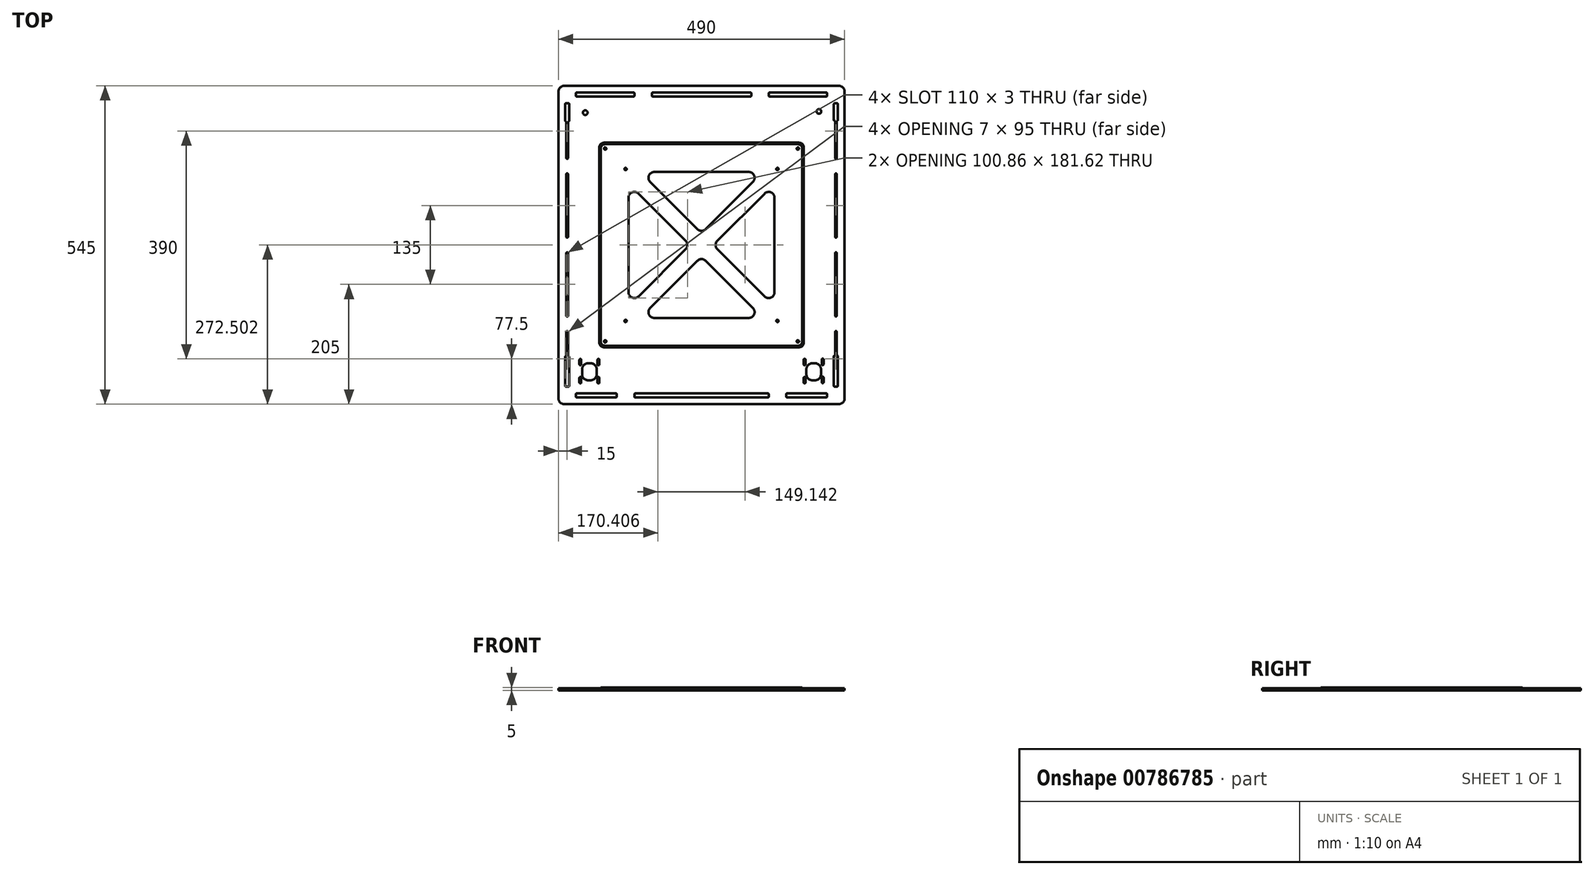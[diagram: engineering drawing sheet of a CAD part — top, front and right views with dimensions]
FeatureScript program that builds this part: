
annotation { "Feature Type Name" : "Feature", "Feature Type Description" : "" }
export const myFeature = defineFeature(function(context is Context, id is Id, definition is map)
    precondition{}
    {
        {
            var Q0;
            Q0=qCreatedBy(makeId("Top.planeOp"),FACE);
            var sketch = newSketch(context, id + "F0", { "sketchPlane" : qUnion([Q0])});
            skLineSegment(sketch, "E0", {"start": v(-83.5, 261) * mm, "end": v(83.54, 261) * mm});
            skLineSegment(sketch, "E1", {"start": v(116.54, 254) * mm, "end": v(213.54, 254) * mm});
            skLineSegment(sketch, "E2", {"start": v(115.04, 259.5) * mm, "end": v(115.04, 255.5) * mm});
            skLineSegment(sketch, "E3", {"start": v(-115, 259.5) * mm, "end": v(-115, 255.5) * mm});
            skArc(sketch, "E4", {"start": v(-226.5, 241) * mm, "mid": v(-226.94, 242.06) * mm, "end": v(-228, 242.5) * mm});
            skLineSegment(sketch, "E5", {"start": v(115, -255.5) * mm, "end": v(115, -259.5) * mm});
            skLineSegment(sketch, "E6", {"start": v(-115, -255.5) * mm, "end": v(-115, -259.5) * mm});
            skLineSegment(sketch, "E7", {"start": v(-179.5, -212.5) * mm, "end": v(-179.5, -221.5) * mm});
            skLineSegment(sketch, "E8", {"start": v(-204.5, -212.5) * mm, "end": v(-204.5, -221.5) * mm});
            skLineSegment(sketch, "E9", {"start": v(-209, -227.5) * mm, "end": v(-209, -235.5) * mm});
            skLineSegment(sketch, "E10", {"start": v(-207.5, -226) * mm, "end": v(-207.4, -226) * mm});
            skArc(sketch, "E11", {"start": v(230, 147.5) * mm, "mid": v(231.06, 147.94) * mm, "end": v(231.5, 149) * mm});
            skLineSegment(sketch, "E12", {"start": v(-205.9, -196.5) * mm, "end": v(-205.9, -204.5) * mm});
            skArc(sketch, "E13", {"start": v(-230, 122.5) * mm, "mid": v(-231.06, 122.06) * mm, "end": v(-231.5, 121) * mm});
            skLineSegment(sketch, "E14", {"start": v(-174.9, -196.5) * mm, "end": v(-174.9, -204.5) * mm});
            skLineSegment(sketch, "E15", {"start": v(-176.5, -206) * mm, "end": v(-176.4, -206) * mm});
            skLineSegment(sketch, "E16", {"start": v(204.5, -212.5) * mm, "end": v(204.5, -221.5) * mm});
            skLineSegment(sketch, "E17", {"start": v(179.5, -212.5) * mm, "end": v(179.5, -221.5) * mm});
            skLineSegment(sketch, "E18", {"start": v(209, -196.07) * mm, "end": v(209, -204.07) * mm});
            skLineSegment(sketch, "E19", {"start": v(207.4, -194.57) * mm, "end": v(207.5, -194.57) * mm});
            skLineSegment(sketch, "E20", {"start": v(178, -227.5) * mm, "end": v(178, -235.5) * mm});
            skLineSegment(sketch, "E21", {"start": v(176.4, -206) * mm, "end": v(176.5, -206) * mm});
            skLineSegment(sketch, "E22", {"start": v(228.5, -189.15) * mm, "end": v(228, -189.15) * mm});
            skLineSegment(sketch, "E23", {"start": v(-233.5, -191.65) * mm, "end": v(-233.5, -241) * mm});
            skLineSegment(sketch, "E24", {"start": v(-226.5, -191.65) * mm, "end": v(-226.5, -241) * mm});
            skLineSegment(sketch, "E25", {"start": v(-228.5, 211.47) * mm, "end": v(-228, 211.47) * mm});
            skLineSegment(sketch, "E26", {"start": v(-228.5, -190.15) * mm, "end": v(-228, -190.15) * mm});
            skLineSegment(sketch, "E27", {"start": v(228, 242.5) * mm, "end": v(232, 242.5) * mm});
            skLineSegment(sketch, "E28", {"start": v(228.5, -189.15) * mm, "end": v(228.5, -149) * mm});
            skLineSegment(sketch, "E29", {"start": v(146.5, -254) * mm, "end": v(213.5, -254) * mm});
            skLineSegment(sketch, "E30", {"start": v(231.5, -189.15) * mm, "end": v(231.5, -149) * mm});
            skLineSegment(sketch, "E31", {"start": v(-228.5, 211.47) * mm, "end": v(-228.5, 149) * mm});
            skLineSegment(sketch, "E32", {"start": v(-245, 262.5) * mm, "end": v(-245, -262.5) * mm});
            skLineSegment(sketch, "E33", {"start": v(245, 262.5) * mm, "end": v(245, -262.5) * mm});
            skLineSegment(sketch, "E34", {"start": v(-235, 272.5) * mm, "end": v(235, 272.5) * mm});
            skLineSegment(sketch, "E35", {"start": v(-213.5, -261) * mm, "end": v(-146.5, -261) * mm});
            skLineSegment(sketch, "E36", {"start": v(232, -242.5) * mm, "end": v(228, -242.5) * mm});
            skLineSegment(sketch, "E37", {"start": v(233.5, -241) * mm, "end": v(233.5, -190.65) * mm});
            skLineSegment(sketch, "E38", {"start": v(215, -255.5) * mm, "end": v(215, -259.5) * mm});
            skLineSegment(sketch, "E39", {"start": v(-226.5, 241) * mm, "end": v(-226.5, 212.97) * mm});
            skLineSegment(sketch, "E40", {"start": v(-172, -241) * mm, "end": v(-172, -194) * mm});
            skLineSegment(sketch, "E41", {"start": v(185, 242.5) * mm, "end": v(185, 222.5) * mm});
            skCircle(sketch, "E42", {"center": v(201, 228.5) * mm, "radius": 4 * mm});
            skLineSegment(sketch, "E43", {"start": v(-215, 205.9) * mm, "end": v(-215, 7.45) * mm});
            skArc(sketch, "E44", {"start": v(-209, -235.5) * mm, "mid": v(-208.56, -236.56) * mm, "end": v(-207.5, -237) * mm});
            skArc(sketch, "E45", {"start": v(-228.5, -14) * mm, "mid": v(-228.94, -12.94) * mm, "end": v(-230, -12.5) * mm});
            skLineSegment(sketch, "E46", {"start": v(-178, -227.5) * mm, "end": v(-178, -235.5) * mm});
            skLineSegment(sketch, "E47", {"start": v(-113.5, -254) * mm, "end": v(113.5, -254) * mm});
            skArc(sketch, "E48", {"start": v(-230, 12.5) * mm, "mid": v(-228.94, 12.94) * mm, "end": v(-228.5, 14) * mm});
            skLineSegment(sketch, "E49", {"start": v(-207.5, -195) * mm, "end": v(-207.4, -195) * mm});
            skArc(sketch, "E50", {"start": v(-228.5, 121) * mm, "mid": v(-228.94, 122.06) * mm, "end": v(-230, 122.5) * mm});
            skArc(sketch, "E51", {"start": v(-83.5, 261) * mm, "mid": v(-84.56, 260.56) * mm, "end": v(-85, 259.5) * mm});
            skArc(sketch, "E52", {"start": v(116.54, 261) * mm, "mid": v(115.48, 260.56) * mm, "end": v(115.04, 259.5) * mm});
            skLineSegment(sketch, "E53", {"start": v(174.9, -227.5) * mm, "end": v(174.9, -235.5) * mm});
            skArc(sketch, "E54", {"start": v(231.5, 121) * mm, "mid": v(231.06, 122.06) * mm, "end": v(230, 122.5) * mm});
            skArc(sketch, "E55", {"start": v(230, 12.5) * mm, "mid": v(231.06, 12.94) * mm, "end": v(231.5, 14) * mm});
            skLineSegment(sketch, "E56", {"start": v(226.5, 214.02) * mm, "end": v(226.5, 241) * mm});
            skLineSegment(sketch, "E57", {"start": v(207.4, -236.57) * mm, "end": v(207.5, -236.57) * mm});
            skArc(sketch, "E58", {"start": v(230, -122.5) * mm, "mid": v(231.06, -122.06) * mm, "end": v(231.5, -121) * mm});
            skArc(sketch, "E59", {"start": v(230, -147.5) * mm, "mid": v(228.94, -147.94) * mm, "end": v(228.5, -149) * mm});
            skArc(sketch, "E60", {"start": v(233.5, -190.65) * mm, "mid": v(233.06, -189.59) * mm, "end": v(232, -189.15) * mm});
            skLineSegment(sketch, "E61", {"start": v(189.5, -202.5) * mm, "end": v(194.5, -202.5) * mm});
            skArc(sketch, "E62", {"start": v(213.5, -261) * mm, "mid": v(214.56, -260.56) * mm, "end": v(215, -259.5) * mm});
            skArc(sketch, "E63", {"start": v(146.5, -254) * mm, "mid": v(145.44, -254.44) * mm, "end": v(145, -255.5) * mm});
            skArc(sketch, "E64", {"start": v(213.5, -192.5) * mm, "mid": v(214.56, -192.06) * mm, "end": v(215, -191) * mm});
            skArc(sketch, "E65", {"start": v(207.4, -225.57) * mm, "mid": v(206.34, -226) * mm, "end": v(205.9, -227.07) * mm});
            skArc(sketch, "E66", {"start": v(-228, 211.47) * mm, "mid": v(-226.94, 211.91) * mm, "end": v(-226.5, 212.97) * mm});
            skArc(sketch, "E67", {"start": v(174.9, -204.5) * mm, "mid": v(175.34, -205.56) * mm, "end": v(176.4, -206) * mm});
            skArc(sketch, "E68", {"start": v(178, -196.5) * mm, "mid": v(177.56, -195.44) * mm, "end": v(176.5, -195) * mm});
            skArc(sketch, "E69", {"start": v(207.5, -205.57) * mm, "mid": v(208.56, -205.13) * mm, "end": v(209, -204.07) * mm});
            skArc(sketch, "E70", {"start": v(-245, -262.5) * mm, "mid": v(-242.07, -269.57) * mm, "end": v(-235, -272.5) * mm});
            skArc(sketch, "E71", {"start": v(-194.5, -202.5) * mm, "mid": v(-201.57, -205.43) * mm, "end": v(-204.5, -212.5) * mm});
            skArc(sketch, "E72", {"start": v(204.5, -212.5) * mm, "mid": v(201.57, -205.43) * mm, "end": v(194.5, -202.5) * mm});
            skArc(sketch, "E73", {"start": v(-195, 212.5) * mm, "mid": v(-187.93, 215.43) * mm, "end": v(-185, 222.5) * mm});
            skArc(sketch, "E74", {"start": v(185, 222.5) * mm, "mid": v(187.93, 215.43) * mm, "end": v(195, 212.5) * mm});
            skLineSegment(sketch, "E75", {"start": v(228.5, -121) * mm, "end": v(228.5, -14) * mm});
            skLineSegment(sketch, "E76", {"start": v(231.5, 149) * mm, "end": v(231.5, 212.52) * mm});
            skLineSegment(sketch, "E77", {"start": v(116.54, 261) * mm, "end": v(213.54, 261) * mm});
            skLineSegment(sketch, "E78", {"start": v(-228.5, 121) * mm, "end": v(-228.5, 14) * mm});
            skArc(sketch, "E79", {"start": v(-172, -194) * mm, "mid": v(-172.44, -192.94) * mm, "end": v(-173.5, -192.5) * mm});
            skLineSegment(sketch, "E80", {"start": v(-83.5, 254) * mm, "end": v(83.54, 254) * mm});
            skLineSegment(sketch, "E81", {"start": v(-85, 259.5) * mm, "end": v(-85, 255.5) * mm});
            skLineSegment(sketch, "E82", {"start": v(-194.5, -202.5) * mm, "end": v(-189.5, -202.5) * mm});
            skLineSegment(sketch, "E83", {"start": v(233.5, 214.02) * mm, "end": v(233.5, 241) * mm});
            skLineSegment(sketch, "E84", {"start": v(-205.9, -227.5) * mm, "end": v(-205.9, -235.5) * mm});
            skLineSegment(sketch, "E85", {"start": v(145, -255.5) * mm, "end": v(145, -259.5) * mm});
            skLineSegment(sketch, "E86", {"start": v(-174.9, -227.5) * mm, "end": v(-174.9, -235.5) * mm});
            skLineSegment(sketch, "E87", {"start": v(207.4, -205.57) * mm, "end": v(207.5, -205.57) * mm});
            skLineSegment(sketch, "E88", {"start": v(-176.5, -237) * mm, "end": v(-176.4, -237) * mm});
            skArc(sketch, "E89", {"start": v(-232, 242.5) * mm, "mid": v(-233.06, 242.06) * mm, "end": v(-233.5, 241) * mm});
            skLineSegment(sketch, "E90", {"start": v(-176.5, -195) * mm, "end": v(-176.4, -195) * mm});
            skLineSegment(sketch, "E91", {"start": v(-207.5, -206) * mm, "end": v(-207.4, -206) * mm});
            skArc(sketch, "E92", {"start": v(-230, 147.5) * mm, "mid": v(-228.94, 147.94) * mm, "end": v(-228.5, 149) * mm});
            skLineSegment(sketch, "E93", {"start": v(231.5, -189.15) * mm, "end": v(228.5, -189.15) * mm});
            skLineSegment(sketch, "E94", {"start": v(-231.5, 211.47) * mm, "end": v(-231.5, 149) * mm});
            skLineSegment(sketch, "E95", {"start": v(189.5, -231.5) * mm, "end": v(194.5, -231.5) * mm});
            skLineSegment(sketch, "E96", {"start": v(231.5, -189.15) * mm, "end": v(232, -189.15) * mm});
            skArc(sketch, "E97", {"start": v(228.5, -121) * mm, "mid": v(228.94, -122.06) * mm, "end": v(230, -122.5) * mm});
            skArc(sketch, "E98", {"start": v(215.04, 259.5) * mm, "mid": v(214.6, 260.56) * mm, "end": v(213.54, 261) * mm});
            skLineSegment(sketch, "E99", {"start": v(176.4, -226) * mm, "end": v(176.5, -226) * mm});
            skLineSegment(sketch, "E100", {"start": v(-233.5, 241) * mm, "end": v(-233.5, 212.97) * mm});
            skLineSegment(sketch, "E101", {"start": v(178, -196.5) * mm, "end": v(178, -204.5) * mm});
            skLineSegment(sketch, "E102", {"start": v(-231.5, -190.15) * mm, "end": v(-232, -190.15) * mm});
            skLineSegment(sketch, "E103", {"start": v(-194.5, -231.5) * mm, "end": v(-189.5, -231.5) * mm});
            skCircle(sketch, "E104", {"center": v(-199, 226.5) * mm, "radius": 4 * mm});
            skLineSegment(sketch, "E105", {"start": v(-195, 212.5) * mm, "end": v(-215, 212.5) * mm});
            skLineSegment(sketch, "E106", {"start": v(-213.5, 261) * mm, "end": v(-116.5, 261) * mm});
            skLineSegment(sketch, "E107", {"start": v(-228.5, -149) * mm, "end": v(-228.5, -190.15) * mm});
            skLineSegment(sketch, "E108", {"start": v(228.5, 14) * mm, "end": v(228.5, 121) * mm});
            skLineSegment(sketch, "E109", {"start": v(215, 212.5) * mm, "end": v(215, 13.22) * mm});
            skLineSegment(sketch, "E110", {"start": v(-231.5, 211.47) * mm, "end": v(-232, 211.47) * mm});
            skLineSegment(sketch, "E111", {"start": v(176.4, -237) * mm, "end": v(176.5, -237) * mm});
            skLineSegment(sketch, "E112", {"start": v(231.5, 212.52) * mm, "end": v(232, 212.52) * mm});
            skLineSegment(sketch, "E113", {"start": v(-207.5, -237) * mm, "end": v(-207.4, -237) * mm});
            skLineSegment(sketch, "E114", {"start": v(-185, 242.5) * mm, "end": v(-185, 222.5) * mm});
            skLineSegment(sketch, "E115", {"start": v(-228, -242.5) * mm, "end": v(-232, -242.5) * mm});
            skLineSegment(sketch, "E116", {"start": v(-213.5, 254) * mm, "end": v(-116.5, 254) * mm});
            skLineSegment(sketch, "E117", {"start": v(-113.5, -261) * mm, "end": v(113.5, -261) * mm});
            skLineSegment(sketch, "E118", {"start": v(-145, -255.5) * mm, "end": v(-145, -259.5) * mm});
            skLineSegment(sketch, "E119", {"start": v(-176.5, -226) * mm, "end": v(-176.4, -226) * mm});
            skArc(sketch, "E120", {"start": v(233.5, 241) * mm, "mid": v(233.06, 242.06) * mm, "end": v(232, 242.5) * mm});
            skArc(sketch, "E121", {"start": v(-230, -122.5) * mm, "mid": v(-228.94, -122.06) * mm, "end": v(-228.5, -121) * mm});
            skArc(sketch, "E122", {"start": v(83.54, 254) * mm, "mid": v(84.6, 254.44) * mm, "end": v(85.04, 255.5) * mm});
            skLineSegment(sketch, "E123", {"start": v(207.4, -225.57) * mm, "end": v(207.5, -225.57) * mm});
            skLineSegment(sketch, "E124", {"start": v(209, -227.07) * mm, "end": v(209, -235.07) * mm});
            skArc(sketch, "E125", {"start": v(228, -189.15) * mm, "mid": v(226.94, -189.59) * mm, "end": v(226.5, -190.65) * mm});
            skArc(sketch, "E126", {"start": v(113.5, -261) * mm, "mid": v(114.56, -260.56) * mm, "end": v(115, -259.5) * mm});
            skArc(sketch, "E127", {"start": v(235, -272.5) * mm, "mid": v(242.07, -269.57) * mm, "end": v(245, -262.5) * mm});
            skArc(sketch, "E128", {"start": v(226.5, 214.02) * mm, "mid": v(226.94, 212.96) * mm, "end": v(228, 212.52) * mm});
            skLineSegment(sketch, "E129", {"start": v(174.9, -196.5) * mm, "end": v(174.9, -204.5) * mm});
            skArc(sketch, "E130", {"start": v(231.5, -14) * mm, "mid": v(231.06, -12.94) * mm, "end": v(230, -12.5) * mm});
            skArc(sketch, "E131", {"start": v(176.4, -226) * mm, "mid": v(175.34, -226.44) * mm, "end": v(174.9, -227.5) * mm});
            skArc(sketch, "E132", {"start": v(-176.5, -195) * mm, "mid": v(-177.56, -195.44) * mm, "end": v(-178, -196.5) * mm});
            skArc(sketch, "E133", {"start": v(178, -227.5) * mm, "mid": v(177.56, -226.44) * mm, "end": v(176.5, -226) * mm});
            skLineSegment(sketch, "E134", {"start": v(-228, 242.5) * mm, "end": v(-232, 242.5) * mm});
            skArc(sketch, "E135", {"start": v(207.4, -194.57) * mm, "mid": v(206.34, -195) * mm, "end": v(205.9, -196.07) * mm});
            skLineSegment(sketch, "E136", {"start": v(-228.5, -14) * mm, "end": v(-228.5, -121) * mm});
            skArc(sketch, "E137", {"start": v(-189.5, -231.5) * mm, "mid": v(-182.43, -228.57) * mm, "end": v(-179.5, -221.5) * mm});
            skArc(sketch, "E138", {"start": v(207.5, -236.57) * mm, "mid": v(208.56, -236.13) * mm, "end": v(209, -235.07) * mm});
            skArc(sketch, "E139", {"start": v(209, -196.07) * mm, "mid": v(208.56, -195) * mm, "end": v(207.5, -194.57) * mm});
            skLineSegment(sketch, "E140", {"start": v(85.04, 259.5) * mm, "end": v(85.04, 255.5) * mm});
            skLineSegment(sketch, "E141", {"start": v(172, -241) * mm, "end": v(172, -194) * mm});
            skArc(sketch, "E142", {"start": v(-174.9, -227.5) * mm, "mid": v(-175.34, -226.44) * mm, "end": v(-176.4, -226) * mm});
            skArc(sketch, "E143", {"start": v(179.5, -221.5) * mm, "mid": v(182.43, -228.57) * mm, "end": v(189.5, -231.5) * mm});
            skLineSegment(sketch, "E144", {"start": v(213.5, -192.5) * mm, "end": v(173.5, -192.5) * mm});
            skLineSegment(sketch, "E145", {"start": v(215.04, 255.5) * mm, "end": v(215.04, 259.5) * mm});
            skLineSegment(sketch, "E146", {"start": v(205.9, -227.07) * mm, "end": v(205.9, -235.07) * mm});
            skLineSegment(sketch, "E147", {"start": v(-178, -196.5) * mm, "end": v(-178, -204.5) * mm});
            skArc(sketch, "E148", {"start": v(-179.5, -212.5) * mm, "mid": v(-182.43, -205.43) * mm, "end": v(-189.5, -202.5) * mm});
            skArc(sketch, "E149", {"start": v(-176.4, -206) * mm, "mid": v(-175.34, -205.56) * mm, "end": v(-174.9, -204.5) * mm});
            skLineSegment(sketch, "E150", {"start": v(231.5, 212.52) * mm, "end": v(228.5, 212.52) * mm});
            skArc(sketch, "E151", {"start": v(-231.5, 149) * mm, "mid": v(-231.06, 147.94) * mm, "end": v(-230, 147.5) * mm});
            skLineSegment(sketch, "E152", {"start": v(215, 212.5) * mm, "end": v(195, 212.5) * mm});
            skArc(sketch, "E153", {"start": v(176.5, -237) * mm, "mid": v(177.56, -236.56) * mm, "end": v(178, -235.5) * mm});
            skArc(sketch, "E154", {"start": v(-204.5, -221.5) * mm, "mid": v(-201.57, -228.57) * mm, "end": v(-194.5, -231.5) * mm});
            skArc(sketch, "E155", {"start": v(230, -12.5) * mm, "mid": v(228.94, -12.94) * mm, "end": v(228.5, -14) * mm});
            skLineSegment(sketch, "E156", {"start": v(205.9, -196.07) * mm, "end": v(205.9, -204.07) * mm});
            skArc(sketch, "E157", {"start": v(-115, 259.5) * mm, "mid": v(-115.44, 260.56) * mm, "end": v(-116.5, 261) * mm});
            skArc(sketch, "E158", {"start": v(231.5, -149) * mm, "mid": v(231.06, -147.94) * mm, "end": v(230, -147.5) * mm});
            skArc(sketch, "E159", {"start": v(174.9, -235.5) * mm, "mid": v(175.34, -236.56) * mm, "end": v(176.4, -237) * mm});
            skArc(sketch, "E160", {"start": v(85.04, 259.5) * mm, "mid": v(84.6, 260.56) * mm, "end": v(83.54, 261) * mm});
            skArc(sketch, "E161", {"start": v(209, -227.07) * mm, "mid": v(208.56, -226) * mm, "end": v(207.5, -225.57) * mm});
            skArc(sketch, "E162", {"start": v(213.54, 254) * mm, "mid": v(214.6, 254.44) * mm, "end": v(215.04, 255.5) * mm});
            skLineSegment(sketch, "E163", {"start": v(176.4, -195) * mm, "end": v(176.5, -195) * mm});
            skArc(sketch, "E164", {"start": v(-176.4, -237) * mm, "mid": v(-175.34, -236.56) * mm, "end": v(-174.9, -235.5) * mm});
            skLineSegment(sketch, "E165", {"start": v(146.5, -261) * mm, "end": v(213.5, -261) * mm});
            skLineSegment(sketch, "E166", {"start": v(-185, 242.5) * mm, "end": v(185, 242.5) * mm});
            skLineSegment(sketch, "E167", {"start": v(-215, 255.5) * mm, "end": v(-215, 259.5) * mm});
            skLineSegment(sketch, "E168", {"start": v(-170.5, -242.5) * mm, "end": v(170.5, -242.5) * mm});
            skArc(sketch, "E169", {"start": v(-215, -259.5) * mm, "mid": v(-214.56, -260.56) * mm, "end": v(-213.5, -261) * mm});
            skLineSegment(sketch, "E170", {"start": v(-209, -196.5) * mm, "end": v(-209, -204.5) * mm});
            skLineSegment(sketch, "E171", {"start": v(-215, -255.5) * mm, "end": v(-215, -259.5) * mm});
            skLineSegment(sketch, "E172", {"start": v(228.5, 212.52) * mm, "end": v(228, 212.52) * mm});
            skLineSegment(sketch, "E173", {"start": v(-231.5, 121) * mm, "end": v(-231.5, 14) * mm});
            skLineSegment(sketch, "E174", {"start": v(228.5, 149) * mm, "end": v(228.5, 212.52) * mm});
            skLineSegment(sketch, "E175", {"start": v(231.5, 14) * mm, "end": v(231.5, 121) * mm});
            skLineSegment(sketch, "E176", {"start": v(231.5, -121) * mm, "end": v(231.5, -14) * mm});
            skLineSegment(sketch, "E177", {"start": v(-231.5, -149) * mm, "end": v(-231.5, -190.15) * mm});
            skArc(sketch, "E178", {"start": v(-228.5, -149) * mm, "mid": v(-228.94, -147.94) * mm, "end": v(-230, -147.5) * mm});
            skLineSegment(sketch, "E179", {"start": v(-231.5, -14) * mm, "end": v(-231.5, -121) * mm});
            skArc(sketch, "E180", {"start": v(245, 262.5) * mm, "mid": v(242.07, 269.57) * mm, "end": v(235, 272.5) * mm});
            skArc(sketch, "E181", {"start": v(-235, 272.5) * mm, "mid": v(-242.07, 269.57) * mm, "end": v(-245, 262.5) * mm});
            skArc(sketch, "E182", {"start": v(189.5, -202.5) * mm, "mid": v(182.43, -205.43) * mm, "end": v(179.5, -212.5) * mm});
            skArc(sketch, "E183", {"start": v(194.5, -231.5) * mm, "mid": v(201.57, -228.57) * mm, "end": v(204.5, -221.5) * mm});
            skArc(sketch, "E184", {"start": v(205.9, -204.07) * mm, "mid": v(206.34, -205.13) * mm, "end": v(207.4, -205.57) * mm});
            skArc(sketch, "E185", {"start": v(176.4, -195) * mm, "mid": v(175.34, -195.44) * mm, "end": v(174.9, -196.5) * mm});
            skArc(sketch, "E186", {"start": v(176.5, -206) * mm, "mid": v(177.56, -205.56) * mm, "end": v(178, -204.5) * mm});
            skArc(sketch, "E187", {"start": v(173.5, -192.5) * mm, "mid": v(172.44, -192.94) * mm, "end": v(172, -194) * mm});
            skArc(sketch, "E188", {"start": v(205.9, -235.07) * mm, "mid": v(206.34, -236.13) * mm, "end": v(207.4, -236.57) * mm});
            skArc(sketch, "E189", {"start": v(170.5, -242.5) * mm, "mid": v(171.56, -242.06) * mm, "end": v(172, -241) * mm});
            skArc(sketch, "E190", {"start": v(226.5, -241) * mm, "mid": v(226.94, -242.06) * mm, "end": v(228, -242.5) * mm});
            skArc(sketch, "E191", {"start": v(145, -259.5) * mm, "mid": v(145.44, -260.56) * mm, "end": v(146.5, -261) * mm});
            skArc(sketch, "E192", {"start": v(215, -255.5) * mm, "mid": v(214.56, -254.44) * mm, "end": v(213.5, -254) * mm});
            skArc(sketch, "E193", {"start": v(232, -242.5) * mm, "mid": v(233.06, -242.06) * mm, "end": v(233.5, -241) * mm});
            skArc(sketch, "E194", {"start": v(228.5, 14) * mm, "mid": v(228.94, 12.94) * mm, "end": v(230, 12.5) * mm});
            skArc(sketch, "E195", {"start": v(230, 122.5) * mm, "mid": v(228.94, 122.06) * mm, "end": v(228.5, 121) * mm});
            skArc(sketch, "E196", {"start": v(228.5, 149) * mm, "mid": v(228.94, 147.94) * mm, "end": v(230, 147.5) * mm});
            skArc(sketch, "E197", {"start": v(232, 212.52) * mm, "mid": v(233.06, 212.96) * mm, "end": v(233.5, 214.02) * mm});
            skArc(sketch, "E198", {"start": v(228, 242.5) * mm, "mid": v(226.94, 242.06) * mm, "end": v(226.5, 241) * mm});
            skArc(sketch, "E199", {"start": v(115.04, 255.5) * mm, "mid": v(115.48, 254.44) * mm, "end": v(116.54, 254) * mm});
            skArc(sketch, "E200", {"start": v(-85, 255.5) * mm, "mid": v(-84.56, 254.44) * mm, "end": v(-83.5, 254) * mm});
            skArc(sketch, "E201", {"start": v(-116.5, 254) * mm, "mid": v(-115.44, 254.44) * mm, "end": v(-115, 255.5) * mm});
            skArc(sketch, "E202", {"start": v(-213.5, 261) * mm, "mid": v(-214.56, 260.56) * mm, "end": v(-215, 259.5) * mm});
            skArc(sketch, "E203", {"start": v(-215, 255.5) * mm, "mid": v(-214.56, 254.44) * mm, "end": v(-213.5, 254) * mm});
            skArc(sketch, "E204", {"start": v(-233.5, 212.97) * mm, "mid": v(-233.06, 211.91) * mm, "end": v(-232, 211.47) * mm});
            skArc(sketch, "E205", {"start": v(-231.5, 14) * mm, "mid": v(-231.06, 12.94) * mm, "end": v(-230, 12.5) * mm});
            skArc(sketch, "E206", {"start": v(-230, -12.5) * mm, "mid": v(-231.06, -12.94) * mm, "end": v(-231.5, -14) * mm});
            skArc(sketch, "E207", {"start": v(-231.5, -121) * mm, "mid": v(-231.06, -122.06) * mm, "end": v(-230, -122.5) * mm});
            skArc(sketch, "E208", {"start": v(-230, -147.5) * mm, "mid": v(-231.06, -147.94) * mm, "end": v(-231.5, -149) * mm});
            skArc(sketch, "E209", {"start": v(-232, -190.15) * mm, "mid": v(-233.06, -190.58) * mm, "end": v(-233.5, -191.65) * mm});
            skArc(sketch, "E210", {"start": v(-226.5, -191.65) * mm, "mid": v(-226.94, -190.58) * mm, "end": v(-228, -190.15) * mm});
            skArc(sketch, "E211", {"start": v(-233.5, -241) * mm, "mid": v(-233.06, -242.06) * mm, "end": v(-232, -242.5) * mm});
            skArc(sketch, "E212", {"start": v(-228, -242.5) * mm, "mid": v(-226.94, -242.06) * mm, "end": v(-226.5, -241) * mm});
            skArc(sketch, "E213", {"start": v(-207.5, -195) * mm, "mid": v(-208.56, -195.44) * mm, "end": v(-209, -196.5) * mm});
            skArc(sketch, "E214", {"start": v(-205.9, -196.5) * mm, "mid": v(-206.34, -195.44) * mm, "end": v(-207.4, -195) * mm});
            skArc(sketch, "E215", {"start": v(-209, -204.5) * mm, "mid": v(-208.56, -205.56) * mm, "end": v(-207.5, -206) * mm});
            skArc(sketch, "E216", {"start": v(-207.4, -206) * mm, "mid": v(-206.34, -205.56) * mm, "end": v(-205.9, -204.5) * mm});
            skArc(sketch, "E217", {"start": v(-215, -191) * mm, "mid": v(-214.56, -192.06) * mm, "end": v(-213.5, -192.5) * mm});
            skArc(sketch, "E218", {"start": v(-178, -204.5) * mm, "mid": v(-177.56, -205.56) * mm, "end": v(-176.5, -206) * mm});
            skArc(sketch, "E219", {"start": v(-174.9, -196.5) * mm, "mid": v(-175.34, -195.44) * mm, "end": v(-176.4, -195) * mm});
            skArc(sketch, "E220", {"start": v(-207.5, -226) * mm, "mid": v(-208.56, -226.44) * mm, "end": v(-209, -227.5) * mm});
            skArc(sketch, "E221", {"start": v(-205.9, -227.5) * mm, "mid": v(-206.34, -226.44) * mm, "end": v(-207.4, -226) * mm});
            skArc(sketch, "E222", {"start": v(-207.4, -237) * mm, "mid": v(-206.34, -236.56) * mm, "end": v(-205.9, -235.5) * mm});
            skArc(sketch, "E223", {"start": v(-178, -235.5) * mm, "mid": v(-177.56, -236.56) * mm, "end": v(-176.5, -237) * mm});
            skArc(sketch, "E224", {"start": v(-176.5, -226) * mm, "mid": v(-177.56, -226.44) * mm, "end": v(-178, -227.5) * mm});
            skArc(sketch, "E225", {"start": v(-172, -241) * mm, "mid": v(-171.56, -242.06) * mm, "end": v(-170.5, -242.5) * mm});
            skArc(sketch, "E226", {"start": v(115, -255.5) * mm, "mid": v(114.56, -254.44) * mm, "end": v(113.5, -254) * mm});
            skArc(sketch, "E227", {"start": v(-113.5, -254) * mm, "mid": v(-114.56, -254.44) * mm, "end": v(-115, -255.5) * mm});
            skArc(sketch, "E228", {"start": v(-115, -259.5) * mm, "mid": v(-114.56, -260.56) * mm, "end": v(-113.5, -261) * mm});
            skArc(sketch, "E229", {"start": v(-146.5, -261) * mm, "mid": v(-145.44, -260.56) * mm, "end": v(-145, -259.5) * mm});
            skArc(sketch, "E230", {"start": v(-145, -255.5) * mm, "mid": v(-145.44, -254.44) * mm, "end": v(-146.5, -254) * mm});
            skArc(sketch, "E231", {"start": v(-213.5, -254) * mm, "mid": v(-214.56, -254.44) * mm, "end": v(-215, -255.5) * mm});
            skLineSegment(sketch, "E232", {"start": v(226.5, -241) * mm, "end": v(226.5, -190.65) * mm});
            skLineSegment(sketch, "E233", {"start": v(-173.5, -192.5) * mm, "end": v(-213.5, -192.5) * mm});
            skLineSegment(sketch, "E234", {"start": v(-213.5, -254) * mm, "end": v(-146.5, -254) * mm});
            skLineSegment(sketch, "E235", {"start": v(-235, -272.5) * mm, "end": v(235, -272.5) * mm});
            skLineSegment(sketch, "E236", {"start": v(175, 167) * mm, "end": v(175, 13.22) * mm});
            skLineSegment(sketch, "E237", {"start": v(-175, 167) * mm, "end": v(-175, 7.45) * mm});
            skCircle(sketch, "E238", {"center": v(165, 165) * mm, "radius": 2 * mm});
            skLineSegment(sketch, "E239", {"start": v(-167, 175) * mm, "end": v(167, 175) * mm});
            skCircle(sketch, "E240", {"center": v(165, -165) * mm, "radius": 2 * mm});
            skLineSegment(sketch, "E241", {"start": v(-167, -175) * mm, "end": v(167, -175) * mm});
            skCircle(sketch, "E242", {"center": v(-165, -165) * mm, "radius": 2 * mm});
            skCircle(sketch, "E243", {"center": v(-165, 165) * mm, "radius": 2 * mm});
            skArc(sketch, "E244", {"start": v(-167, 175) * mm, "mid": v(-172.66, 172.66) * mm, "end": v(-175, 167) * mm});
            skArc(sketch, "E245", {"start": v(175, 167) * mm, "mid": v(172.66, 172.66) * mm, "end": v(167, 175) * mm});
            skArc(sketch, "E246", {"start": v(167, -175) * mm, "mid": v(172.66, -172.66) * mm, "end": v(175, -167) * mm});
            skArc(sketch, "E247", {"start": v(-175, -167) * mm, "mid": v(-172.66, -172.66) * mm, "end": v(-167, -175) * mm});
            skLineSegment(sketch, "E248.trimOffspring", {"start": v(-215, 2.45) * mm, "end": v(-215, -191) * mm});
            skLineSegment(sketch, "E249.trimOffspring", {"start": v(-175, 2.45) * mm, "end": v(-175, -167) * mm});
            skLineSegment(sketch, "E250.trimOffspring", {"start": v(175, 8.22) * mm, "end": v(175, -167) * mm});
            skLineSegment(sketch, "E251.trimOffspring", {"start": v(215, 8.22) * mm, "end": v(215, -191) * mm});
            skLineSegment(sketch, "E252", {"start": v(-215, 205.9) * mm, "end": v(-215, 212.5) * mm});
            skLineSegment(sketch, "E253", {"start": v(-175, 2.45) * mm, "end": v(-175, 7.45) * mm});
            skLineSegment(sketch, "E254", {"start": v(175, 8.22) * mm, "end": v(175, 13.22) * mm});
            skSolve(sketch);
        }
        {
            var Q0;
            Q0=makeQuery(id+"F0.imprint","IMPRINT",FACE,{"disambiguationData":[TD([[makeQuery(id+"F0.imprint","IMPRINT",EDGE,{"derivedFrom":sQuery(id+"F0.wireOp",EDGE,"E0")}),1.0]])]});
            extrude(context, id + "F1", {"entities" : qUnion([Q0]), "depth" : 4 * mm});
        }
        {
            var Q0;
            Q0=makeQuery(id+"F0.imprint","IMPRINT",FACE,{"disambiguationData":[TD([[makeQuery(id+"F0.imprint","IMPRINT",EDGE,{"derivedFrom":sQuery(id+"F0.wireOp",EDGE,"E236")}),-1.0]])]});
            extrude(context, id + "F2", {"entities" : qUnion([Q0]), "depth" : 3 * mm, "offsetDistance" : 25 * mm});
        }
        {
            var Q0;
            Q0=qCreatedBy(makeId("Top.planeOp"),FACE);
            var sketch = newSketch(context, id + "F3", { "sketchPlane" : qUnion([Q0])});
            skCircle(sketch, "E255", {"center": v(-165.02, 165) * mm, "radius": 2 * mm});
            skCircle(sketch, "E256", {"center": v(164.98, 165) * mm, "radius": 2 * mm});
            skCircle(sketch, "E257", {"center": v(-165.02, -165) * mm, "radius": 2 * mm});
            skCircle(sketch, "E258", {"center": v(164.98, -165) * mm, "radius": 2 * mm});
            skArc(sketch, "E259", {"start": v(172.48, 165) * mm, "mid": v(170.27, 170.31) * mm, "end": v(164.95, 172.5) * mm});
            skArc(sketch, "E260", {"start": v(-165.02, 172.5) * mm, "mid": v(-170.33, 170.3) * mm, "end": v(-172.52, 165) * mm});
            skArc(sketch, "E261", {"start": v(-172.52, -165) * mm, "mid": v(-170.33, -170.3) * mm, "end": v(-165.02, -172.5) * mm});
            skArc(sketch, "E262", {"start": v(164.98, -172.5) * mm, "mid": v(170.28, -170.3) * mm, "end": v(172.48, -165) * mm});
            skLineSegment(sketch, "E263", {"start": v(164.98, -172.5) * mm, "end": v(-165.02, -172.5) * mm});
            skLineSegment(sketch, "E264", {"start": v(172.48, -165) * mm, "end": v(172.48, 165) * mm});
            skLineSegment(sketch, "E265", {"start": v(-172.52, -165) * mm, "end": v(-172.52, 165) * mm});
            skLineSegment(sketch, "E266", {"start": v(164.95, 172.5) * mm, "end": v(-165.02, 172.5) * mm});
            skCircle(sketch, "E267", {"center": v(-130.02, 130) * mm, "radius": 2 * mm});
            skCircle(sketch, "E268", {"center": v(129.98, 130) * mm, "radius": 2 * mm});
            skCircle(sketch, "E269", {"center": v(129.98, -130) * mm, "radius": 2 * mm});
            skCircle(sketch, "E270", {"center": v(-130.02, -130) * mm, "radius": 2 * mm});
            skLineSegment(sketch, "E271.bottom", {"start": v(-80.88, 125) * mm, "end": v(80.84, 125) * mm});
            skLineSegment(sketch, "E271.top", {"start": v(-80.88, -125) * mm, "end": v(80.84, -125) * mm});
            skLineSegment(sketch, "E271.left", {"start": v(-125.02, 80.86) * mm, "end": v(-125.02, -80.86) * mm});
            skLineSegment(sketch, "E271.right", {"start": v(124.98, 80.86) * mm, "end": v(124.98, -80.86) * mm});
            skPoint(sketch, "E272.visualSharp", {"position": v(124.98, 125) * mm});
            skPoint(sketch, "E273.visualSharp", {"position": v(-125.02, 125) * mm});
            skPoint(sketch, "E274.visualSharp", {"position": v(124.98, -125) * mm});
            skPoint(sketch, "E275.visualSharp", {"position": v(-125.02, -125) * mm});
            skLineSegment(sketch, "E276", {"start": v(-107.95, 87.93) * mm, "end": v(-27.1, 7.07) * mm});
            skLineSegment(sketch, "E277", {"start": v(-87.95, 107.93) * mm, "end": v(-7.1, 27.07) * mm});
            skLineSegment(sketch, "E278", {"start": v(87.9, 107.93) * mm, "end": v(7.05, 27.07) * mm});
            skLineSegment(sketch, "E279", {"start": v(107.9, 87.93) * mm, "end": v(27.05, 7.07) * mm});
            skLineSegment(sketch, "E280.trimOffspring", {"start": v(27.05, -7.07) * mm, "end": v(107.9, -87.93) * mm});
            skLineSegment(sketch, "E281.trimOffspring", {"start": v(-27.1, -7.07) * mm, "end": v(-107.95, -87.93) * mm});
            skLineSegment(sketch, "E282.trimOffspring", {"start": v(7.05, -27.07) * mm, "end": v(87.9, -107.93) * mm});
            skLineSegment(sketch, "E283.trimOffspring", {"start": v(-7.1, -27.07) * mm, "end": v(-87.95, -107.93) * mm});
            skPoint(sketch, "E284.visualSharp", {"position": v(-0.02, 20) * mm});
            skArc(sketch, "E284.filletArc", {"start": v(-7.1, 27.07) * mm, "mid": v(-0.02, 24.14) * mm, "end": v(7.05, 27.07) * mm});
            skPoint(sketch, "E285.visualSharp", {"position": v(-20.02, 0) * mm});
            skArc(sketch, "E285.filletArc", {"start": v(-27.1, -7.07) * mm, "mid": v(-24.16, 0) * mm, "end": v(-27.1, 7.07) * mm});
            skPoint(sketch, "E286.visualSharp", {"position": v(-0.02, -20) * mm});
            skArc(sketch, "E286.filletArc", {"start": v(7.05, -27.07) * mm, "mid": v(-0.02, -24.14) * mm, "end": v(-7.1, -27.07) * mm});
            skPoint(sketch, "E287.visualSharp", {"position": v(19.98, 0) * mm});
            skArc(sketch, "E287.filletArc", {"start": v(27.05, 7.07) * mm, "mid": v(24.12, 0) * mm, "end": v(27.05, -7.07) * mm});
            skPoint(sketch, "E288.visualSharp", {"position": v(124.98, 105) * mm});
            skArc(sketch, "E288.filletArc", {"start": v(124.98, 80.86) * mm, "mid": v(118.8, 90.1) * mm, "end": v(107.9, 87.93) * mm});
            skPoint(sketch, "E289.visualSharp", {"position": v(104.98, 125) * mm});
            skArc(sketch, "E289.filletArc", {"start": v(87.9, 107.93) * mm, "mid": v(90.07, 118.83) * mm, "end": v(80.84, 125) * mm});
            skPoint(sketch, "E290.visualSharp", {"position": v(-105.02, 125) * mm});
            skArc(sketch, "E290.filletArc", {"start": v(-80.88, 125) * mm, "mid": v(-90.12, 118.83) * mm, "end": v(-87.95, 107.93) * mm});
            skPoint(sketch, "E291.visualSharp", {"position": v(-125.02, 105) * mm});
            skArc(sketch, "E291.filletArc", {"start": v(-107.95, 87.93) * mm, "mid": v(-118.85, 90.1) * mm, "end": v(-125.02, 80.86) * mm});
            skPoint(sketch, "E292.visualSharp", {"position": v(-125.02, -105) * mm});
            skArc(sketch, "E292.filletArc", {"start": v(-125.02, -80.86) * mm, "mid": v(-118.85, -90.1) * mm, "end": v(-107.95, -87.93) * mm});
            skPoint(sketch, "E293.visualSharp", {"position": v(-105.02, -125) * mm});
            skArc(sketch, "E293.filletArc", {"start": v(-87.95, -107.93) * mm, "mid": v(-90.12, -118.83) * mm, "end": v(-80.88, -125) * mm});
            skPoint(sketch, "E294.visualSharp", {"position": v(104.98, -125) * mm});
            skArc(sketch, "E294.filletArc", {"start": v(80.84, -125) * mm, "mid": v(90.07, -118.83) * mm, "end": v(87.9, -107.93) * mm});
            skPoint(sketch, "E295.visualSharp", {"position": v(124.98, -105) * mm});
            skArc(sketch, "E295.filletArc", {"start": v(107.9, -87.93) * mm, "mid": v(118.8, -90.1) * mm, "end": v(124.98, -80.86) * mm});
            skSolve(sketch);
        }
        {
            var Q0;
            Q0 = qSketchRegion(id + "F3", true);
            extrude(context, id + "F4", {"entities" : qUnion([Q0]), "depth" : 5 * mm, "offsetDistance" : 25 * mm});
        }
    });
